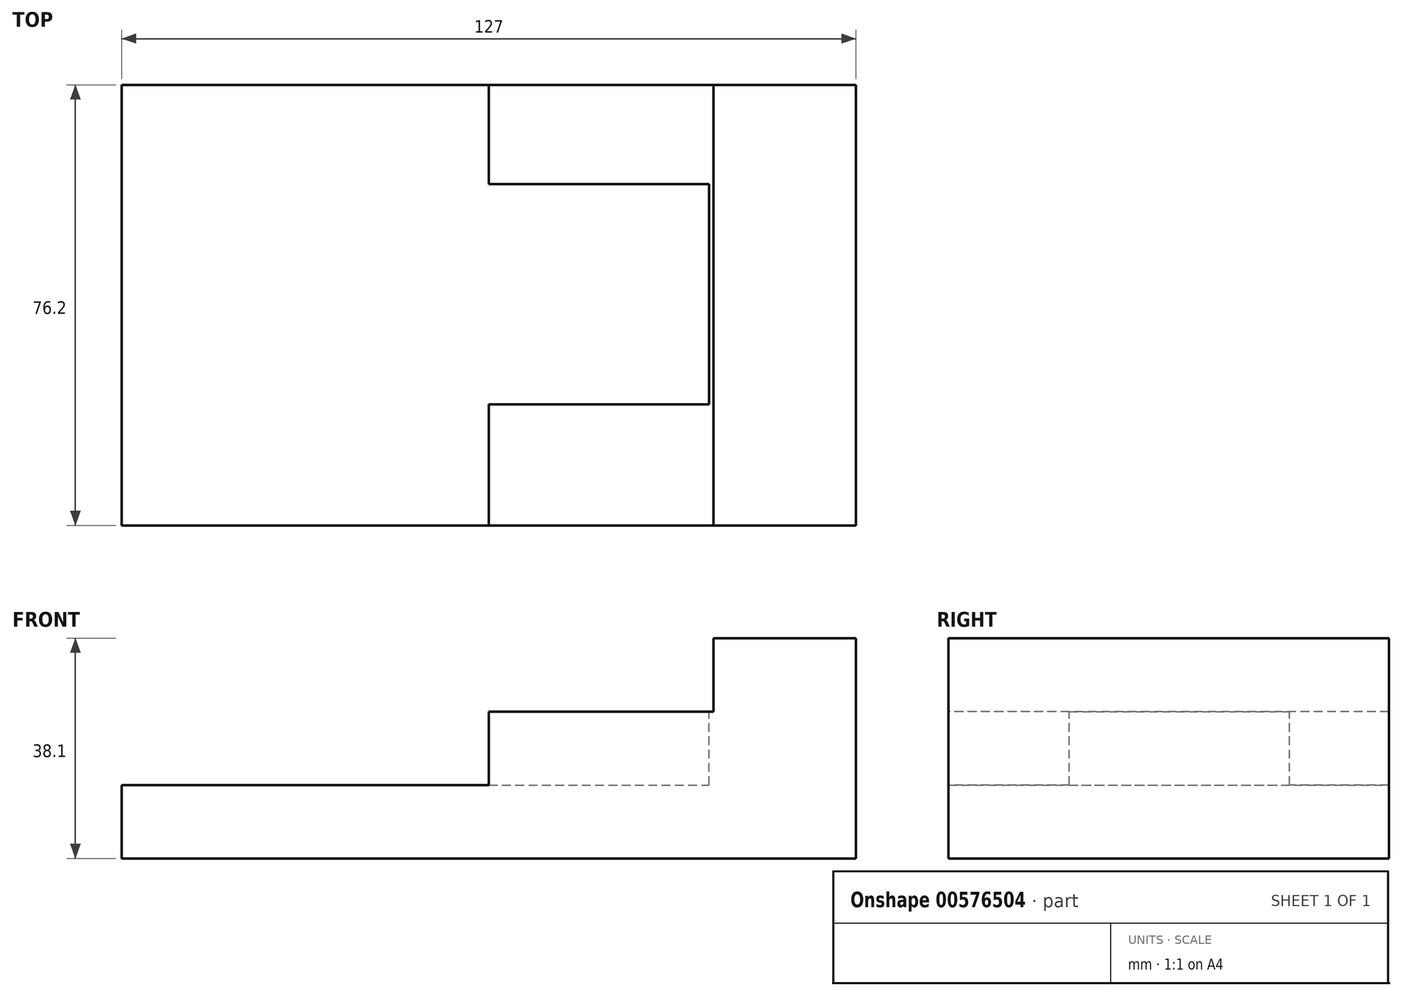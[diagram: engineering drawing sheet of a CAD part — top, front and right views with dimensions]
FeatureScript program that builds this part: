
annotation { "Feature Type Name" : "Feature", "Feature Type Description" : "" }
export const myFeature = defineFeature(function(context is Context, id is Id, definition is map)
    precondition{}
    {
        {
            var Q0;
            Q0=qCreatedBy(makeId("Top.planeOp"),FACE);
            var sketch = newSketch(context, id + "F0", { "sketchPlane" : qUnion([Q0])});
            skLineSegment(sketch, "E0.bottom", {"start": v(63.5, -38.1) * mm, "end": v(-63.5, -38.1) * mm});
            skLineSegment(sketch, "E0.top", {"start": v(63.5, 38.1) * mm, "end": v(-63.5, 38.1) * mm});
            skLineSegment(sketch, "E0.left", {"start": v(63.5, -38.1) * mm, "end": v(63.5, 38.1) * mm});
            skLineSegment(sketch, "E0.right", {"start": v(-63.5, -38.1) * mm, "end": v(-63.5, 38.1) * mm});
            skPoint(sketch, "E0.middle", {"position": v(0, 0) * mm});
            skSolve(sketch);
        }
        {
            var Q0;
            Q0=makeQuery(id+"F0.imprint","IMPRINT",FACE,{"disambiguationData":[TD([[makeQuery(id+"F0.imprint","IMPRINT",EDGE,{"derivedFrom":sQuery(id+"F0.wireOp",EDGE,"E0.bottom")}),-1.0]])]});
            extrude(context, id + "F1", {"entities" : qUnion([Q0]), "depth" : 12.7 * mm, "offsetDistance" : 25.4 * mm});
        }
        {
            var Q0;
            Q0=makeQuery(id+"F1.opExtrude","CAP_FACE",FACE,{"disambiguationData":[OSD([sQuery(id+"F0.wireOp",EDGE,"E0.bottom"),sQuery(id+"F0.wireOp",EDGE,"E0.top"),sQuery(id+"F0.wireOp",EDGE,"E0.left"),sQuery(id+"F0.wireOp",EDGE,"E0.right")])],"isStart":false});
            var sketch = newSketch(context, id + "F2", { "sketchPlane" : qUnion([Q0])});
            skLineSegment(sketch, "E1.bottom", {"start": v(0, 38.1) * mm, "end": v(63.5, 38.1) * mm});
            skLineSegment(sketch, "E1.top", {"start": v(0, -38.1) * mm, "end": v(63.5, -38.1) * mm});
            skLineSegment(sketch, "E1.left", {"start": v(0, 38.1) * mm, "end": v(0, -38.1) * mm});
            skLineSegment(sketch, "E1.right", {"start": v(63.5, 38.1) * mm, "end": v(63.5, -38.1) * mm});
            skSolve(sketch);
        }
        {
            var Q0;
            Q0=makeQuery(id+"F2.imprint","IMPRINT",FACE,{"disambiguationData":[TD([[makeQuery(id+"F2.imprint","IMPRINT",EDGE,{"derivedFrom":sQuery(id+"F2.wireOp",EDGE,"E1.bottom")}),1.0]])]});
            extrude(context, id + "F3", {"entities" : qUnion([Q0]), "operationType" : NewBodyOperationType.ADD, "depth" : 12.7 * mm, "offsetDistance" : 25.4 * mm});
        }
        {
            var Q0;
            Q0=makeQuery(id+"F3.opExtrude","CAP_FACE",FACE,{"disambiguationData":[OSD([sQuery(id+"F2.wireOp",EDGE,"E1.bottom"),sQuery(id+"F2.wireOp",EDGE,"E1.top"),sQuery(id+"F2.wireOp",EDGE,"E1.left"),sQuery(id+"F2.wireOp",EDGE,"E1.right")])],"isStart":false});
            var sketch = newSketch(context, id + "F4", { "sketchPlane" : qUnion([Q0])});
            skLineSegment(sketch, "E2.bottom", {"start": v(0, -17.2) * mm, "end": v(38.1, -17.2) * mm});
            skLineSegment(sketch, "E2.top", {"start": v(0, 20.9) * mm, "end": v(38.1, 20.9) * mm});
            skLineSegment(sketch, "E2.left", {"start": v(0, -17.2) * mm, "end": v(0, 20.9) * mm});
            skLineSegment(sketch, "E2.right", {"start": v(38.1, -17.2) * mm, "end": v(38.1, 20.9) * mm});
            skSolve(sketch);
        }
        {
            var Q0;
            Q0 = qSketchRegion(id + "F4", true);
            extrude(context, id + "F5", {"entities" : qUnion([Q0]), "operationType" : NewBodyOperationType.REMOVE, "oppositeDirection" : true, "depth" : 12.7 * mm, "offsetDistance" : 25.4 * mm});
        }
        {
            var Q0;
            Q0=makeQuery(id+"F3.opExtrude","CAP_FACE",FACE,{"disambiguationData":[OSD([sQuery(id+"F2.wireOp",EDGE,"E1.bottom"),sQuery(id+"F2.wireOp",EDGE,"E1.top"),sQuery(id+"F2.wireOp",EDGE,"E1.left"),sQuery(id+"F2.wireOp",EDGE,"E1.right")])],"isStart":false});
            var sketch = newSketch(context, id + "F6", { "sketchPlane" : qUnion([Q0])});
            skLineSegment(sketch, "E3.bottom", {"start": v(38.86, 38.1) * mm, "end": v(63.5, 38.1) * mm});
            skLineSegment(sketch, "E3.top", {"start": v(38.86, -38.1) * mm, "end": v(63.5, -38.1) * mm});
            skLineSegment(sketch, "E3.left", {"start": v(38.86, 38.1) * mm, "end": v(38.86, -38.1) * mm});
            skLineSegment(sketch, "E3.right", {"start": v(63.5, 38.1) * mm, "end": v(63.5, -38.1) * mm});
            skSolve(sketch);
        }
        {
            var Q0;
            Q0=makeQuery(id+"F6.imprint","IMPRINT",FACE,{"disambiguationData":[TD([[makeQuery(id+"F6.imprint","IMPRINT",EDGE,{"derivedFrom":sQuery(id+"F6.wireOp",EDGE,"E3.bottom")}),1.0]])]});
            extrude(context, id + "F7", {"entities" : qUnion([Q0]), "operationType" : NewBodyOperationType.ADD, "depth" : 12.7 * mm, "offsetDistance" : 25.4 * mm});
        }
    });
